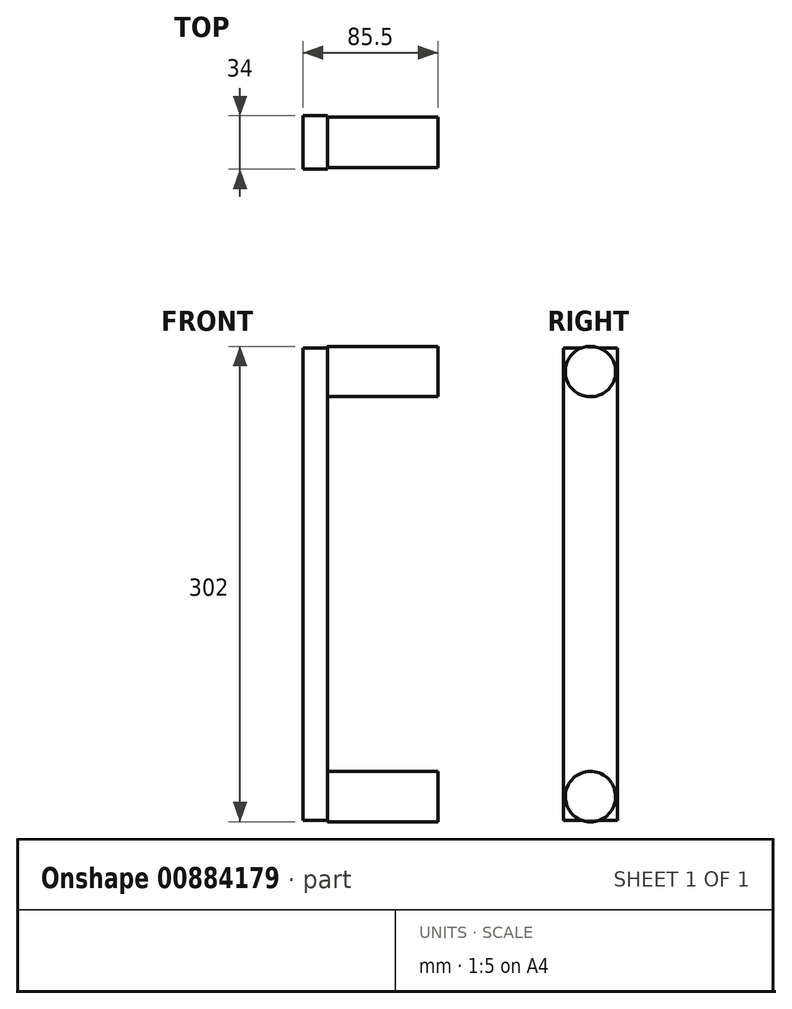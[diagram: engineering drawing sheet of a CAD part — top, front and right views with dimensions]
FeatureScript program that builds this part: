
annotation { "Feature Type Name" : "Feature", "Feature Type Description" : "" }
export const myFeature = defineFeature(function(context is Context, id is Id, definition is map)
    precondition{}
    {
        {
            var Q0;
            Q0=qCreatedBy(makeId("Top.planeOp"),FACE);
            var sketch = newSketch(context, id + "F0", { "sketchPlane" : qUnion([Q0])});
            skLineSegment(sketch, "E0.bottom", {"start": v(0, 0) * mm, "end": v(15.5, 0) * mm});
            skLineSegment(sketch, "E0.top", {"start": v(0, -34) * mm, "end": v(15.5, -34) * mm});
            skLineSegment(sketch, "E0.left", {"start": v(0, 0) * mm, "end": v(0, -34) * mm});
            skLineSegment(sketch, "E0.right", {"start": v(15.5, 0) * mm, "end": v(15.5, -34) * mm});
            skSolve(sketch);
        }
        {
            var Q0;
            Q0=qSketchRegion(id+"F0",true);
            extrude(context, id + "F1", {"entities" : qUnion([Q0]), "depth" : 300 * mm, "offsetDistance" : 25 * mm});
        }
        {
            var Q0;
            Q0=makeQuery(id+"F1.opExtrude","SWEPT_FACE",FACE,{"disambiguationData":[OSD([sQuery(id+"F0.wireOp",EDGE,"E0.right")])]});
            var sketch = newSketch(context, id + "F2", { "sketchPlane" : qUnion([Q0])});
            skLineSegment(sketch, "E1", {"start": v(-17, 300) * mm, "end": v(-17, 0) * mm, "construction": true});
            skCircle(sketch, "E2", {"center": v(-17, 285) * mm, "radius": 16 * mm});
            skLineSegment(sketch, "E3", {"start": v(-34, 150) * mm, "end": v(0, 150) * mm, "construction": true});
            skCircle(sketch, "E4.MirrorC", {"center": v(-17, 15) * mm, "radius": 16 * mm});
            skSolve(sketch);
        }
        {
            var Q0;
            Q0 = qSketchRegion(id + "F2", true);
            extrude(context, id + "F3", {"entities" : qUnion([Q0]), "operationType" : NewBodyOperationType.ADD, "depth" : 70 * mm, "offsetDistance" : 25 * mm});
        }
    });
